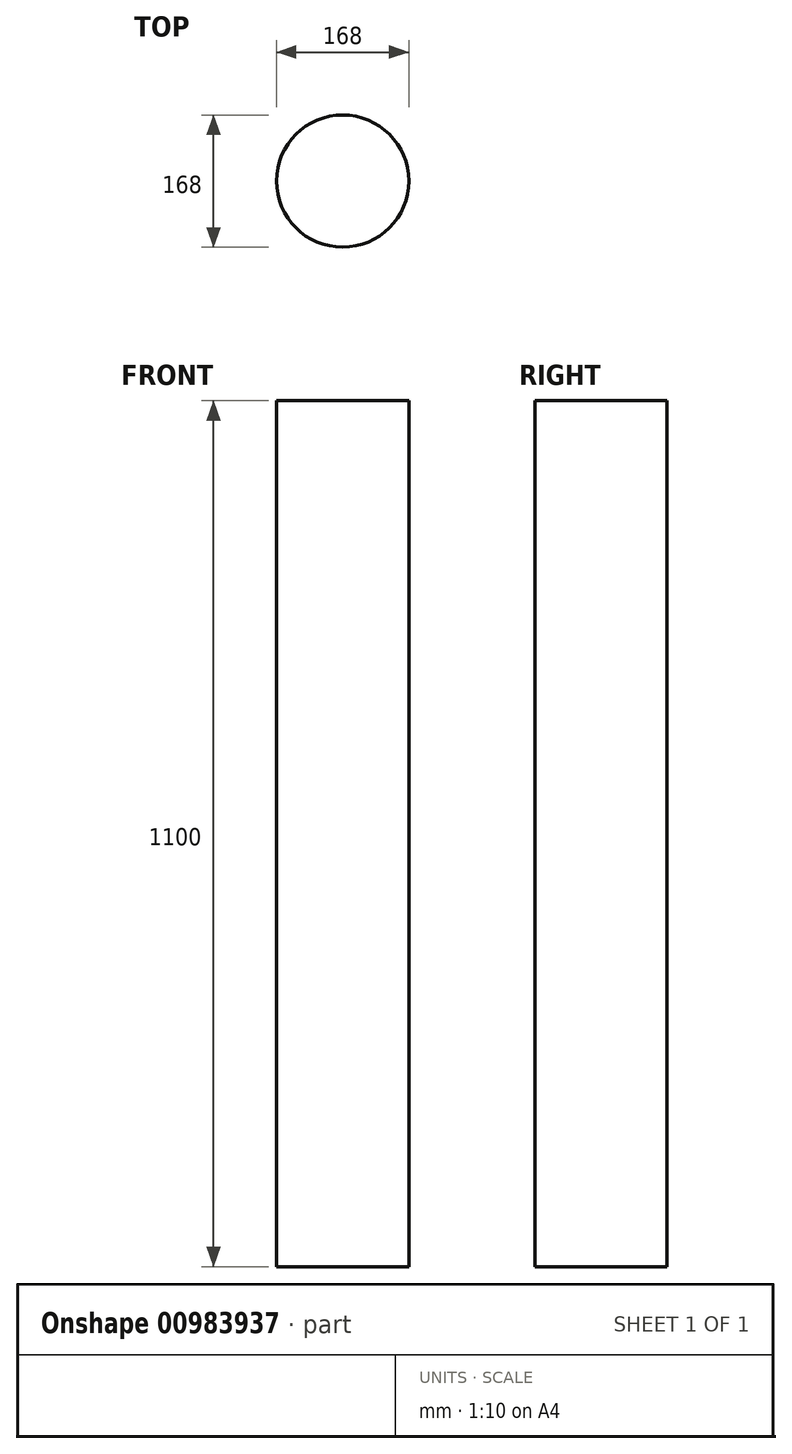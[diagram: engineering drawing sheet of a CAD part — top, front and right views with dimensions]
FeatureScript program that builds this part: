
annotation { "Feature Type Name" : "Feature", "Feature Type Description" : "" }
export const myFeature = defineFeature(function(context is Context, id is Id, definition is map)
    precondition{}
    {
        {
            var Q0;
            Q0=qCreatedBy(makeId("Top.planeOp"),FACE);
            var sketch = newSketch(context, id + "F0", { "sketchPlane" : qUnion([Q0])});
            skCircle(sketch, "E0", {"center": v(0, 0) * mm, "radius": 84 * mm});
            skSolve(sketch);
        }
        {
            var Q0;
            Q0=makeQuery(id+"F0.imprint","IMPRINT",FACE,{"disambiguationData":[TD([[makeQuery(id+"F0.imprint","IMPRINT",EDGE,{"derivedFrom":sQuery(id+"F0.wireOp",EDGE,"E0")}),1.0]])]});
            extrude(context, id + "F1", {"entities" : qUnion([Q0]), "depth" : 1100 * mm, "offsetDistance" : 25 * mm});
        }
    });
